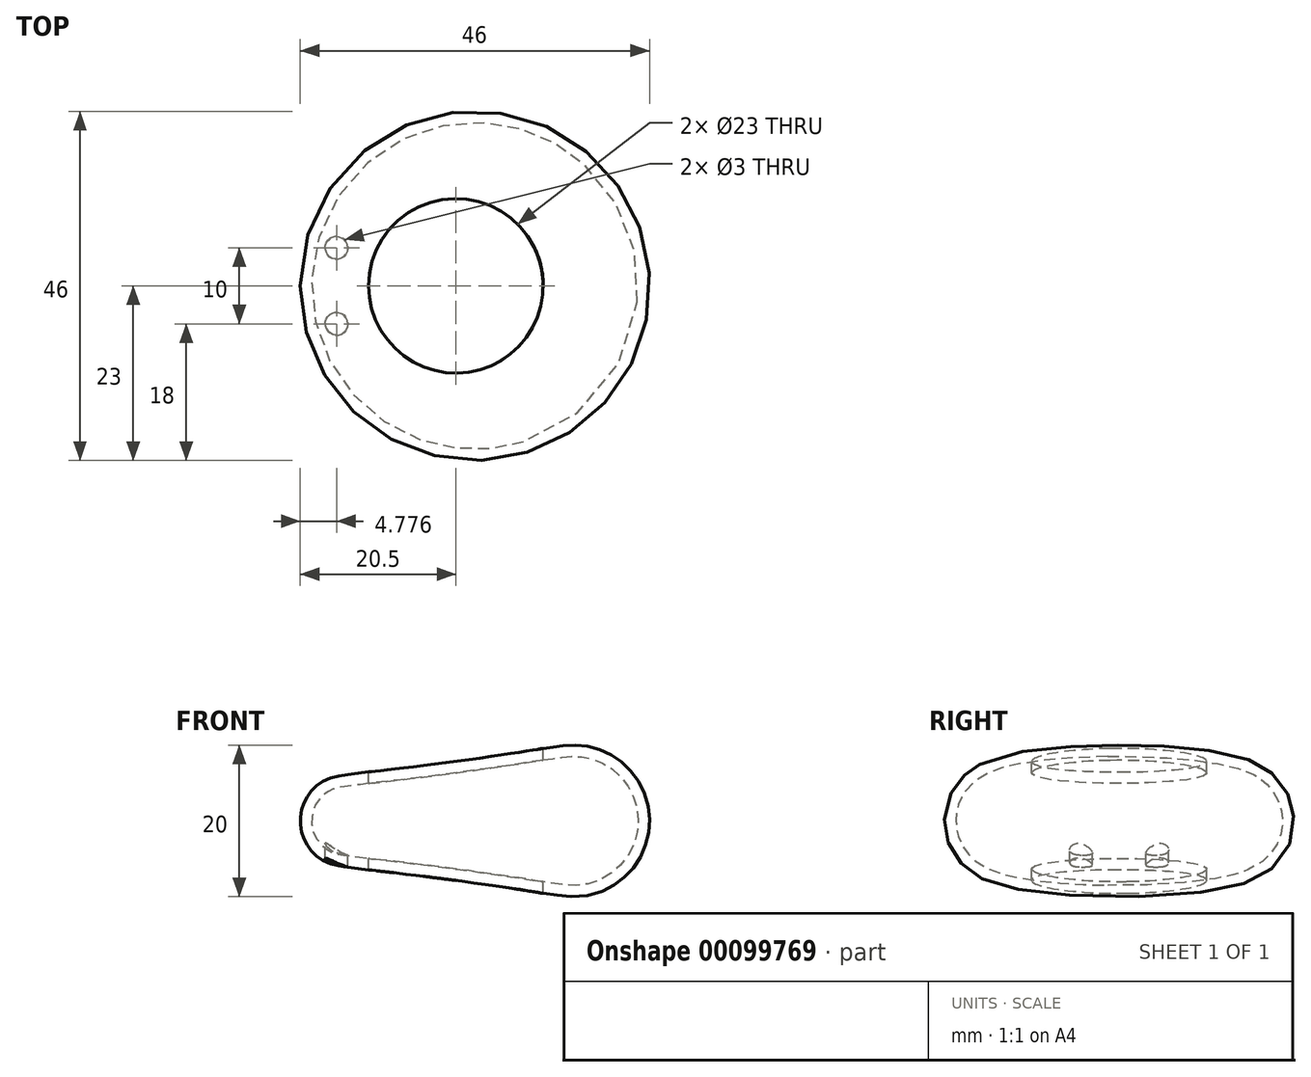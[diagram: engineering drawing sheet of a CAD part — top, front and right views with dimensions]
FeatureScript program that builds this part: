
annotation { "Feature Type Name" : "Feature", "Feature Type Description" : "" }
export const myFeature = defineFeature(function(context is Context, id is Id, definition is map)
    precondition{}
    {
        {
            var Q0;
            Q0=qCreatedBy(makeId("Front.planeOp"),FACE);
            var sketch = newSketch(context, id + "F0", { "sketchPlane" : qUnion([Q0])});
            skArc(sketch, "E0", {"start": v(-17.8, 5.95) * mm, "mid": v(-23, 0) * mm, "end": v(-17.8, -5.95) * mm});
            skArc(sketch, "E1", {"start": v(11.67, -9.91) * mm, "mid": v(23, 0) * mm, "end": v(11.67, 9.91) * mm});
            skLineSegment(sketch, "E2", {"start": v(11.67, 9.91) * mm, "end": v(2, 8.61) * mm});
            skLineSegment(sketch, "E3", {"start": v(-17.8, -5.95) * mm, "end": v(-8, -7.26) * mm});
            skLineSegment(sketch, "E4", {"start": v(2, 8.61) * mm, "end": v(2, -8.61) * mm});
            skLineSegment(sketch, "E5", {"start": v(-8, 7.26) * mm, "end": v(-8, -7.26) * mm});
            skLineSegment(sketch, "E6.trimOffspring", {"start": v(-8, 7.26) * mm, "end": v(-17.8, 5.95) * mm});
            skLineSegment(sketch, "E7.trimOffspring", {"start": v(2, -8.61) * mm, "end": v(11.67, -9.91) * mm});
            skLineSegment(sketch, "E8", {"start": v(-3, 17.48) * mm, "end": v(-3, -13.44) * mm, "construction": true});
            skSolve(sketch);
        }
        {
            var Q0;
            Q0=qCreatedBy(makeId("Top.planeOp"),FACE);
            var sketch = newSketch(context, id + "F1", { "sketchPlane" : qUnion([Q0])});
            skCircle(sketch, "E9", {"center": v(0, 0) * mm, "radius": 23 * mm});
            skCircle(sketch, "E10", {"center": v(-2, 0) * mm, "radius": 15 * mm});
            skCircle(sketch, "E11", {"center": v(-3, 0) * mm, "radius": 5 * mm});
            skSolve(sketch);
        }
        {
            var Q0;
            Q0=makeQuery(id+"F0.imprint","IMPRINT",FACE,{"disambiguationData":[TD([[makeQuery(id+"F0.imprint","IMPRINT",EDGE,{"derivedFrom":sQuery(id+"F0.wireOp",EDGE,"E0")}),1.0]])]});
            var Q1;
            Q1=makeQuery(id+"F0.imprint","IMPRINT",FACE,{"disambiguationData":[TD([[makeQuery(id+"F0.imprint","IMPRINT",EDGE,{"derivedFrom":sQuery(id+"F0.wireOp",EDGE,"E1")}),1.0]])]});
            var Q2;
            Q2=sQuery(id+"F1.wireOp",EDGE,"E9");
            var Q3;
            Q3=sQuery(id+"F1.wireOp",EDGE,"E11");
            loft(context, id + "F2", {"addGuides" : true, "sheetProfilesArray" : [{ "sheetProfileEntities" : qUnion([Q0]) }, { "sheetProfileEntities" : qUnion([Q1]) }], "guidesArray" : [{ "guideEntities" : qUnion([Q2]), "guideDerivativeType" : LoftGuideDerivativeType.DEFAULT, "guideDerivativeMagnitude" : 1 }, { "guideEntities" : qUnion([Q3]), "guideDerivativeType" : LoftGuideDerivativeType.DEFAULT, "guideDerivativeMagnitude" : 1 }]});
        }
        {
            var Q0;
            Q0=qCreatedBy(makeId("Top.planeOp"),FACE);
            var sketch = newSketch(context, id + "F3", { "sketchPlane" : qUnion([Q0])});
            skCircle(sketch, "E12", {"center": v(-2.5, 0) * mm, "radius": 11.5 * mm});
            skSolve(sketch);
        }
        {
            var Q0;
            Q0 = qSketchRegion(id + "F3", true);
            extrude(context, id + "F4", {"entities" : qUnion([Q0]), "operationType" : NewBodyOperationType.REMOVE, "endBound" : BoundingType.SYMMETRIC, "oppositeDirection" : true, "depth" : 25 * mm});
        }
        {
            var Q0;
            Q0=makeQuery(id+"F4.boolean.opBoolean","COPY",FACE,{"derivedFrom":makeQuery(id+"F4.opExtrude","SWEPT_FACE",FACE,{"disambiguationData":[OSD([sQuery(id+"F3.wireOp",EDGE,"E12")])]})});
            shell(context, id + "F5", {"entities" : qUnion([Q0]), "thickness" : 1.5 * mm});
        }
        {
            var Q0;
            Q0=qCreatedBy(makeId("Top.planeOp"),FACE);
            var sketch = newSketch(context, id + "F6", { "sketchPlane" : qUnion([Q0])});
            skLineSegment(sketch, "E13.bottom", {"start": v(-58.37, 46.45) * mm, "end": v(-32.1, 46.45) * mm});
            skLineSegment(sketch, "E13.top", {"start": v(-58.37, 63.26) * mm, "end": v(-32.1, 63.26) * mm});
            skLineSegment(sketch, "E13.left", {"start": v(-58.37, 46.45) * mm, "end": v(-58.37, 63.26) * mm});
            skLineSegment(sketch, "E13.right", {"start": v(-32.1, 46.45) * mm, "end": v(-32.1, 63.26) * mm});
            skSolve(sketch);
        }
        {
            var Q0;
            Q0=makeQuery(id+"F6.imprint","IMPRINT",FACE,{"disambiguationData":[TD([[makeQuery(id+"F6.imprint","IMPRINT",EDGE,{"derivedFrom":sQuery(id+"F6.wireOp",EDGE,"E13.bottom")}),1.0]])]});
            extrude(context, id + "F7", {"entities" : qUnion([Q0]), "depth" : 25 * mm});
        }
        {
            var Q0;
            Q0=makeQuery(id+"F7.opExtrude","CAP_EDGE",EDGE,{"disambiguationData":[OSD([sQuery(id+"F6.wireOp",EDGE,"E13.top")])],"isStart":false});
            fillet(context, id + "F8", {"entities" : qUnion([Q0]), "radius" : 5 * mm, "tangentPropagation" : true, "allowEdgeOverflow" : false});
        }
        {
            var Q0;
            Q0=makeQuery(id+"F7.opExtrude","SWEPT_BODY",BODY,{"disambiguationData":[OSD([sQuery(id+"F6.wireOp",EDGE,"E13.bottom"),sQuery(id+"F6.wireOp",EDGE,"E13.top"),sQuery(id+"F6.wireOp",EDGE,"E13.left"),sQuery(id+"F6.wireOp",EDGE,"E13.right")])]});
            deleteBodies(context, id + "F9", {"entities" : qUnion([Q0])});
        }
        {
            var Q0;
            Q0=qCreatedBy(makeId("Top.planeOp"),FACE);
            var sketch = newSketch(context, id + "F10", { "sketchPlane" : qUnion([Q0])});
            skCircle(sketch, "E14", {"center": v(-18.22, -5) * mm, "radius": 1.5 * mm});
            skCircle(sketch, "E15.MirrorC", {"center": v(-18.22, 5) * mm, "radius": 1.5 * mm});
            skSolve(sketch);
        }
        {
            var Q0;
            Q0 = qSketchRegion(id + "F10", true);
            extrude(context, id + "F11", {"entities" : qUnion([Q0]), "operationType" : NewBodyOperationType.REMOVE, "oppositeDirection" : true, "offsetDistance" : 25 * mm, "depth" : 25 * mm});
        }
    });
